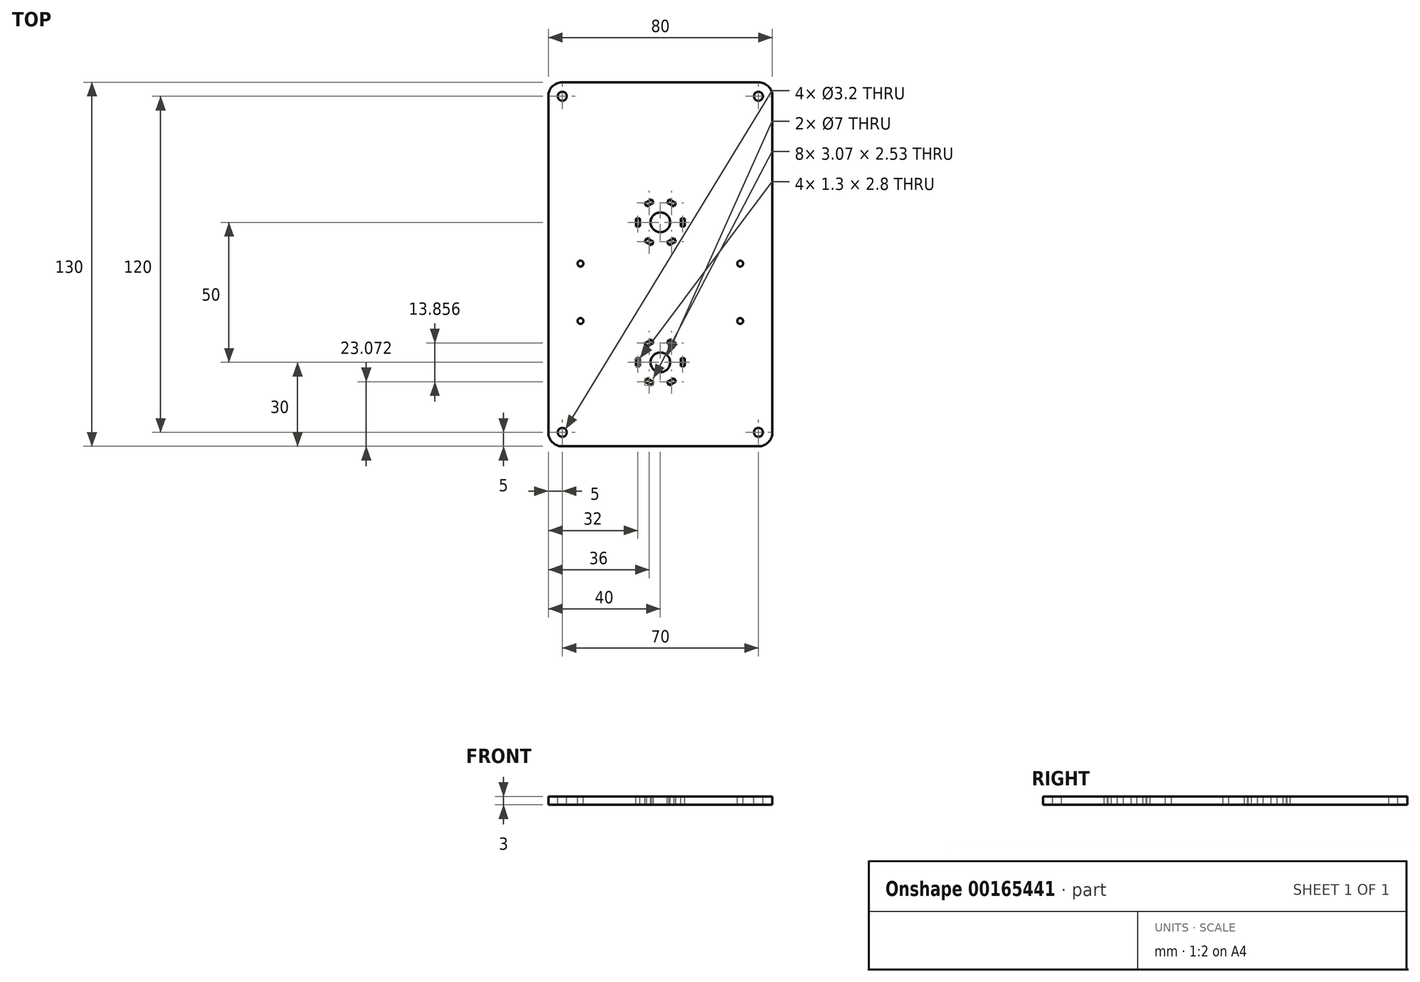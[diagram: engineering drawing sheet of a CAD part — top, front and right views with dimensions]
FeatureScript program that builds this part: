
annotation { "Feature Type Name" : "Feature", "Feature Type Description" : "" }
export const myFeature = defineFeature(function(context is Context, id is Id, definition is map)
    precondition{}
    {
        {
            var Q0;
            Q0=qCreatedBy(makeId("Top.planeOp"),FACE);
            var sketch = newSketch(context, id + "F0", { "sketchPlane" : qUnion([Q0])});
            skLineSegment(sketch, "E0.bottom", {"start": v(-35, 65) * mm, "end": v(35, 65) * mm});
            skLineSegment(sketch, "E0.top", {"start": v(-35, -65) * mm, "end": v(35, -65) * mm});
            skLineSegment(sketch, "E0.left", {"start": v(-40, 60) * mm, "end": v(-40, -60) * mm});
            skLineSegment(sketch, "E0.right", {"start": v(40, 60) * mm, "end": v(40, -60) * mm});
            skPoint(sketch, "E1", {"position": v(-40, 0) * mm});
            skPoint(sketch, "E2", {"position": v(0, 65) * mm});
            skPoint(sketch, "E3.visualSharp", {"position": v(-40, 65) * mm});
            skArc(sketch, "E3.filletArc", {"start": v(-35, 65) * mm, "mid": v(-38.54, 63.54) * mm, "end": v(-40, 60) * mm});
            skPoint(sketch, "E4.visualSharp", {"position": v(40, 65) * mm});
            skArc(sketch, "E4.filletArc", {"start": v(40, 60) * mm, "mid": v(38.54, 63.54) * mm, "end": v(35, 65) * mm});
            skPoint(sketch, "E5.visualSharp", {"position": v(-40, -65) * mm});
            skArc(sketch, "E5.filletArc", {"start": v(-40, -60) * mm, "mid": v(-38.54, -63.54) * mm, "end": v(-35, -65) * mm});
            skPoint(sketch, "E6.visualSharp", {"position": v(40, -65) * mm});
            skArc(sketch, "E6.filletArc", {"start": v(35, -65) * mm, "mid": v(38.54, -63.54) * mm, "end": v(40, -60) * mm});
            skSolve(sketch);
        }
        {
            var Q0;
            Q0 = qSketchRegion(id + "F0", true);
            extrude(context, id + "F1", {"entities" : qUnion([Q0]), "depth" : 3 * mm});
        }
        {
            var Q0;
            Q0=makeQuery(id+"F1.opExtrude","CAP_FACE",FACE,{"disambiguationData":[OSD([sQuery(id+"F0.wireOp",EDGE,"E0.bottom"),sQuery(id+"F0.wireOp",EDGE,"E0.top"),sQuery(id+"F0.wireOp",EDGE,"E0.left"),sQuery(id+"F0.wireOp",EDGE,"E0.right"),sQuery(id+"F0.wireOp",EDGE,"E3.filletArc"),sQuery(id+"F0.wireOp",EDGE,"E4.filletArc"),sQuery(id+"F0.wireOp",EDGE,"E5.filletArc"),sQuery(id+"F0.wireOp",EDGE,"E6.filletArc")])],"isStart":false});
            var sketch = newSketch(context, id + "F2", { "sketchPlane" : qUnion([Q0])});
            skCircle(sketch, "E7", {"center": v(0, 15) * mm, "radius": 3.5 * mm});
            skCircle(sketch, "E8", {"center": v(0, -35) * mm, "radius": 3.5 * mm});
            skLineSegment(sketch, "E9.bottom", {"start": v(-8.65, 16.4) * mm, "end": v(-7.35, 16.4) * mm});
            skLineSegment(sketch, "E9.top", {"start": v(-8.65, 13.6) * mm, "end": v(-7.35, 13.6) * mm});
            skLineSegment(sketch, "E9.left", {"start": v(-8.65, 16.4) * mm, "end": v(-8.65, 13.6) * mm});
            skLineSegment(sketch, "E9.right", {"start": v(-7.35, 16.4) * mm, "end": v(-7.35, 13.6) * mm});
            skPoint(sketch, "E10", {"position": v(-7.35, 15) * mm});
            skLineSegment(sketch, "E11", {"start": v(-7.35, 15) * mm, "end": v(-8.65, 15) * mm, "construction": true});
            skPoint(sketch, "E12", {"position": v(-8, 15) * mm});
            skPoint(sketch, "E13.1.0", {"position": v(-3.67, 21.37) * mm});
            skPoint(sketch, "E13.1.1", {"position": v(-4, 21.93) * mm});
            skLineSegment(sketch, "E13.1.2", {"start": v(-3.11, 23.2) * mm, "end": v(-5.54, 21.8) * mm});
            skLineSegment(sketch, "E13.1.3", {"start": v(-2.46, 22.07) * mm, "end": v(-4.89, 20.67) * mm});
            skLineSegment(sketch, "E13.1.4", {"start": v(-3.68, 21.37) * mm, "end": v(-4.33, 22.5) * mm, "construction": true});
            skLineSegment(sketch, "E13.1.5", {"start": v(-3.11, 23.2) * mm, "end": v(-2.46, 22.07) * mm});
            skLineSegment(sketch, "E13.1.6", {"start": v(-5.54, 21.8) * mm, "end": v(-4.89, 20.67) * mm});
            skPoint(sketch, "E13.2.0", {"position": v(3.67, 21.37) * mm});
            skPoint(sketch, "E13.2.1", {"position": v(4, 21.93) * mm});
            skLineSegment(sketch, "E13.2.2", {"start": v(5.54, 21.8) * mm, "end": v(3.11, 23.2) * mm});
            skLineSegment(sketch, "E13.2.3", {"start": v(4.89, 20.67) * mm, "end": v(2.46, 22.07) * mm});
            skLineSegment(sketch, "E13.2.4", {"start": v(3.67, 21.37) * mm, "end": v(4.32, 22.5) * mm, "construction": true});
            skLineSegment(sketch, "E13.2.5", {"start": v(5.54, 21.8) * mm, "end": v(4.89, 20.67) * mm});
            skLineSegment(sketch, "E13.2.6", {"start": v(3.11, 23.2) * mm, "end": v(2.46, 22.07) * mm});
            skPoint(sketch, "E13.3.0", {"position": v(7.35, 15) * mm});
            skPoint(sketch, "E13.3.1", {"position": v(8, 15) * mm});
            skLineSegment(sketch, "E13.3.2", {"start": v(8.65, 13.6) * mm, "end": v(8.65, 16.4) * mm});
            skLineSegment(sketch, "E13.3.3", {"start": v(7.35, 13.6) * mm, "end": v(7.35, 16.4) * mm});
            skLineSegment(sketch, "E13.3.4", {"start": v(7.35, 15) * mm, "end": v(8.65, 15) * mm, "construction": true});
            skLineSegment(sketch, "E13.3.5", {"start": v(8.65, 13.6) * mm, "end": v(7.35, 13.6) * mm});
            skLineSegment(sketch, "E13.3.6", {"start": v(8.65, 16.4) * mm, "end": v(7.35, 16.4) * mm});
            skPoint(sketch, "E13.4.0", {"position": v(3.68, 8.63) * mm});
            skPoint(sketch, "E13.4.1", {"position": v(4, 8.07) * mm});
            skLineSegment(sketch, "E13.4.2", {"start": v(3.11, 6.8) * mm, "end": v(5.54, 8.2) * mm});
            skLineSegment(sketch, "E13.4.3", {"start": v(2.46, 7.93) * mm, "end": v(4.89, 9.33) * mm});
            skLineSegment(sketch, "E13.4.4", {"start": v(3.68, 8.63) * mm, "end": v(4.33, 7.5) * mm, "construction": true});
            skLineSegment(sketch, "E13.4.5", {"start": v(3.11, 6.8) * mm, "end": v(2.46, 7.93) * mm});
            skLineSegment(sketch, "E13.4.6", {"start": v(5.54, 8.2) * mm, "end": v(4.89, 9.33) * mm});
            skPoint(sketch, "E13.5.0", {"position": v(-3.67, 8.63) * mm});
            skPoint(sketch, "E13.5.1", {"position": v(-4, 8.07) * mm});
            skLineSegment(sketch, "E13.5.2", {"start": v(-5.54, 8.2) * mm, "end": v(-3.11, 6.8) * mm});
            skLineSegment(sketch, "E13.5.3", {"start": v(-4.89, 9.33) * mm, "end": v(-2.46, 7.93) * mm});
            skLineSegment(sketch, "E13.5.4", {"start": v(-3.68, 8.63) * mm, "end": v(-4.33, 7.5) * mm, "construction": true});
            skLineSegment(sketch, "E13.5.5", {"start": v(-5.54, 8.2) * mm, "end": v(-4.89, 9.33) * mm});
            skLineSegment(sketch, "E13.5.6", {"start": v(-3.11, 6.8) * mm, "end": v(-2.46, 7.93) * mm});
            skLineSegment(sketch, "E13.anchor1", {"start": v(0, 15) * mm, "end": v(-8.65, 13.6) * mm, "construction": true});
            skLineSegment(sketch, "E13.anchor2", {"start": v(0, 15) * mm, "end": v(-3.11, 6.8) * mm, "construction": true});
            skLineSegment(sketch, "E14.bottom", {"start": v(-8.65, -33.6) * mm, "end": v(-7.35, -33.6) * mm});
            skLineSegment(sketch, "E14.top", {"start": v(-8.65, -36.4) * mm, "end": v(-7.35, -36.4) * mm});
            skLineSegment(sketch, "E14.left", {"start": v(-8.65, -33.6) * mm, "end": v(-8.65, -36.4) * mm});
            skLineSegment(sketch, "E14.right", {"start": v(-7.35, -33.6) * mm, "end": v(-7.35, -36.4) * mm});
            skPoint(sketch, "E15", {"position": v(-7.35, -35) * mm});
            skLineSegment(sketch, "E16.1.0", {"start": v(-5.54, -41.8) * mm, "end": v(-3.11, -43.2) * mm});
            skPoint(sketch, "E16.1.1", {"position": v(-3.67, -41.37) * mm});
            skLineSegment(sketch, "E16.1.2", {"start": v(-4.89, -40.67) * mm, "end": v(-2.46, -42.07) * mm});
            skLineSegment(sketch, "E16.1.3", {"start": v(-5.54, -41.8) * mm, "end": v(-4.89, -40.67) * mm});
            skLineSegment(sketch, "E16.1.4", {"start": v(-3.11, -43.2) * mm, "end": v(-2.46, -42.07) * mm});
            skLineSegment(sketch, "E16.2.0", {"start": v(3.11, -43.2) * mm, "end": v(5.54, -41.8) * mm});
            skPoint(sketch, "E16.2.1", {"position": v(3.67, -41.37) * mm});
            skLineSegment(sketch, "E16.2.2", {"start": v(2.46, -42.07) * mm, "end": v(4.89, -40.67) * mm});
            skLineSegment(sketch, "E16.2.3", {"start": v(3.11, -43.2) * mm, "end": v(2.46, -42.07) * mm});
            skLineSegment(sketch, "E16.2.4", {"start": v(5.54, -41.8) * mm, "end": v(4.89, -40.67) * mm});
            skLineSegment(sketch, "E16.3.0", {"start": v(8.65, -36.4) * mm, "end": v(8.65, -33.6) * mm});
            skPoint(sketch, "E16.3.1", {"position": v(7.35, -35) * mm});
            skLineSegment(sketch, "E16.3.2", {"start": v(7.35, -36.4) * mm, "end": v(7.35, -33.6) * mm});
            skLineSegment(sketch, "E16.3.3", {"start": v(8.65, -36.4) * mm, "end": v(7.35, -36.4) * mm});
            skLineSegment(sketch, "E16.3.4", {"start": v(8.65, -33.6) * mm, "end": v(7.35, -33.6) * mm});
            skLineSegment(sketch, "E16.4.0", {"start": v(5.54, -28.2) * mm, "end": v(3.11, -26.8) * mm});
            skPoint(sketch, "E16.4.1", {"position": v(3.68, -28.63) * mm});
            skLineSegment(sketch, "E16.4.2", {"start": v(4.89, -29.33) * mm, "end": v(2.46, -27.93) * mm});
            skLineSegment(sketch, "E16.4.3", {"start": v(5.54, -28.2) * mm, "end": v(4.89, -29.33) * mm});
            skLineSegment(sketch, "E16.4.4", {"start": v(3.11, -26.8) * mm, "end": v(2.46, -27.93) * mm});
            skLineSegment(sketch, "E16.5.0", {"start": v(-3.11, -26.8) * mm, "end": v(-5.54, -28.2) * mm});
            skPoint(sketch, "E16.5.1", {"position": v(-3.67, -28.63) * mm});
            skLineSegment(sketch, "E16.5.2", {"start": v(-2.46, -27.93) * mm, "end": v(-4.89, -29.33) * mm});
            skLineSegment(sketch, "E16.5.3", {"start": v(-3.11, -26.8) * mm, "end": v(-2.46, -27.93) * mm});
            skLineSegment(sketch, "E16.5.4", {"start": v(-5.54, -28.2) * mm, "end": v(-4.89, -29.33) * mm});
            skCircle(sketch, "E17", {"center": v(0, 15) * mm, "radius": 15.5 * mm, "construction": true});
            skCircle(sketch, "E18", {"center": v(0, -35) * mm, "radius": 15.5 * mm, "construction": true});
            skSolve(sketch);
        }
        {
            var Q0;
            Q0 = qSketchRegion(id + "F2", true);
            extrude(context, id + "F3", {"entities" : qUnion([Q0]), "operationType" : NewBodyOperationType.REMOVE, "endBound" : BoundingType.THROUGH_ALL, "oppositeDirection" : true, "depth" : 25 * mm});
        }
        {
            var Q0;
            Q0=makeQuery(id+"F1.opExtrude","CAP_FACE",FACE,{"disambiguationData":[OSD([sQuery(id+"F0.wireOp",EDGE,"E0.bottom"),sQuery(id+"F0.wireOp",EDGE,"E0.top"),sQuery(id+"F0.wireOp",EDGE,"E0.left"),sQuery(id+"F0.wireOp",EDGE,"E0.right"),sQuery(id+"F0.wireOp",EDGE,"E3.filletArc"),sQuery(id+"F0.wireOp",EDGE,"E4.filletArc"),sQuery(id+"F0.wireOp",EDGE,"E5.filletArc"),sQuery(id+"F0.wireOp",EDGE,"E6.filletArc")])],"isStart":false});
            var sketch = newSketch(context, id + "F4", { "sketchPlane" : qUnion([Q0])});
            skCircle(sketch, "E19", {"center": v(-28.5, 0.25) * mm, "radius": 1.05 * mm});
            skLineSegment(sketch, "E20.bottom", {"start": v(-28.5, 0.25) * mm, "end": v(28.5, 0.25) * mm, "construction": true});
            skLineSegment(sketch, "E20.top", {"start": v(-28.5, -20.25) * mm, "end": v(28.5, -20.25) * mm, "construction": true});
            skLineSegment(sketch, "E20.left", {"start": v(-28.5, 0.25) * mm, "end": v(-28.5, -20.25) * mm, "construction": true});
            skLineSegment(sketch, "E20.right", {"start": v(28.5, 0.25) * mm, "end": v(28.5, -20.25) * mm, "construction": true});
            skLineSegment(sketch, "E21", {"start": v(0, 15) * mm, "end": v(0, -35) * mm, "construction": true});
            skPoint(sketch, "E22", {"position": v(-28.5, -10) * mm});
            skPoint(sketch, "E23", {"position": v(0, -10) * mm});
            skCircle(sketch, "E24", {"center": v(28.5, 0.25) * mm, "radius": 1.05 * mm});
            skCircle(sketch, "E25", {"center": v(28.5, -20.25) * mm, "radius": 1.05 * mm});
            skCircle(sketch, "E26", {"center": v(-28.5, -20.25) * mm, "radius": 1.05 * mm});
            skPoint(sketch, "E27", {"position": v(0, 0.25) * mm});
            skCircle(sketch, "E28", {"center": v(-35, 60) * mm, "radius": 1.6 * mm});
            skCircle(sketch, "E29", {"center": v(35, 60) * mm, "radius": 1.6 * mm});
            skCircle(sketch, "E30", {"center": v(35, -60) * mm, "radius": 1.6 * mm});
            skCircle(sketch, "E31", {"center": v(-35, -60) * mm, "radius": 1.6 * mm});
            skSolve(sketch);
        }
        {
            var Q0;
            Q0 = qSketchRegion(id + "F4", true);
            extrude(context, id + "F5", {"entities" : qUnion([Q0]), "operationType" : NewBodyOperationType.REMOVE, "endBound" : BoundingType.THROUGH_ALL, "oppositeDirection" : true, "depth" : 25 * mm});
        }
    });
